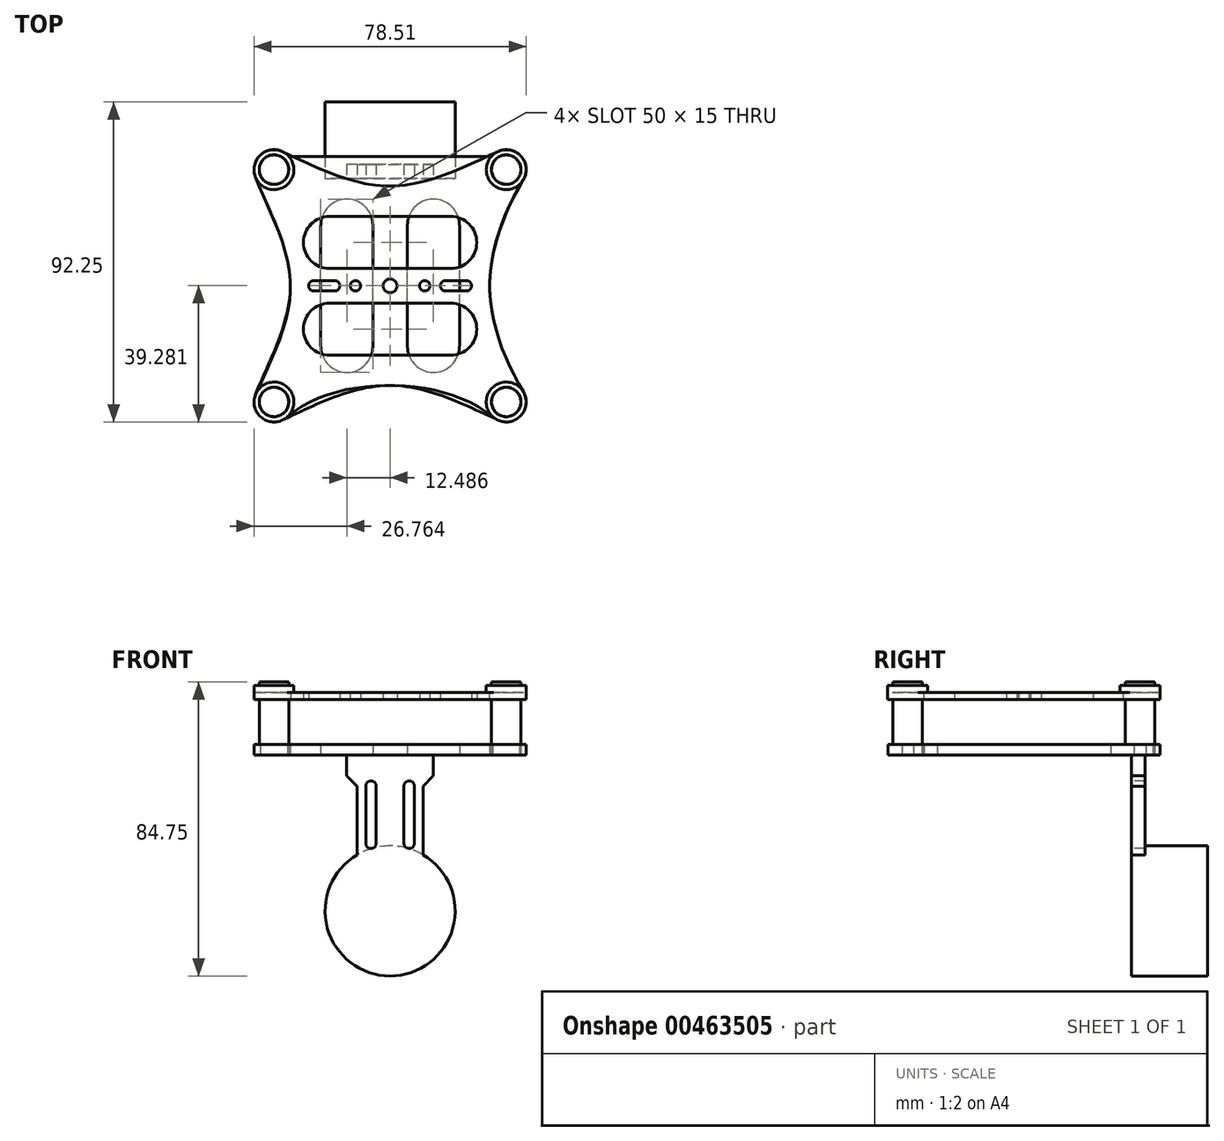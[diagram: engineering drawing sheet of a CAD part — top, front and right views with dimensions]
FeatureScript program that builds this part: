
annotation { "Feature Type Name" : "Feature", "Feature Type Description" : "" }
export const myFeature = defineFeature(function(context is Context, id is Id, definition is map)
    precondition{}
    {
        {
            var Q0;
            Q0=qCreatedBy(makeId("Top.planeOp"),FACE);
            var sketch = newSketch(context, id + "F0", { "sketchPlane" : qUnion([Q0])});
            skCircle(sketch, "E0", {"center": v(0, 0) * mm, "radius": 2 * mm});
            skCircle(sketch, "E1", {"center": v(10, 0) * mm, "radius": 1.5 * mm});
            skCircle(sketch, "E2", {"center": v(-10, 0) * mm, "radius": 1.5 * mm});
            skCircle(sketch, "E3", {"center": v(16, 0) * mm, "radius": 1.5 * mm});
            skCircle(sketch, "E4", {"center": v(22, 0) * mm, "radius": 1.5 * mm});
            skCircle(sketch, "E5", {"center": v(-16, 0) * mm, "radius": 1.5 * mm});
            skCircle(sketch, "E6", {"center": v(-22, 0) * mm, "radius": 1.5 * mm});
            skLineSegment(sketch, "E7", {"start": v(-22, 1.5) * mm, "end": v(-16, 1.5) * mm});
            skLineSegment(sketch, "E8", {"start": v(-22, -1.5) * mm, "end": v(-16, -1.5) * mm});
            skLineSegment(sketch, "E9", {"start": v(16, 1.5) * mm, "end": v(22, 1.5) * mm});
            skLineSegment(sketch, "E10", {"start": v(16, -1.5) * mm, "end": v(22, -1.5) * mm});
            skCircle(sketch, "E11", {"center": v(17.5, 12.5) * mm, "radius": 7.5 * mm});
            skCircle(sketch, "E12", {"center": v(-17.5, 12.5) * mm, "radius": 7.5 * mm});
            skCircle(sketch, "E13", {"center": v(-17.5, -12.5) * mm, "radius": 7.5 * mm});
            skCircle(sketch, "E14", {"center": v(17.5, -12.5) * mm, "radius": 7.5 * mm});
            skLineSegment(sketch, "E15", {"start": v(-17.5, 20) * mm, "end": v(17.5, 20) * mm});
            skLineSegment(sketch, "E16", {"start": v(-17.5, 5) * mm, "end": v(17.5, 5) * mm});
            skLineSegment(sketch, "E17", {"start": v(-17.5, -5) * mm, "end": v(17.5, -5) * mm});
            skLineSegment(sketch, "E18", {"start": v(-17.5, -20) * mm, "end": v(17.5, -20) * mm});
            skLineSegment(sketch, "E19.bottom", {"start": v(-39.25, 39.25) * mm, "end": v(39.25, 39.25) * mm});
            skLineSegment(sketch, "E19.top", {"start": v(-39.25, -39.25) * mm, "end": v(39.25, -39.25) * mm});
            skLineSegment(sketch, "E19.left", {"start": v(-39.25, 39.25) * mm, "end": v(-39.25, -39.25) * mm});
            skLineSegment(sketch, "E19.right", {"start": v(39.25, 39.25) * mm, "end": v(39.25, -39.25) * mm});
            skCircle(sketch, "E20", {"center": v(33.5, 33.5) * mm, "radius": 4.25 * mm});
            skCircle(sketch, "E21", {"center": v(33.5, 33.5) * mm, "radius": 5.75 * mm});
            skCircle(sketch, "E22", {"center": v(-33.5, 33.5) * mm, "radius": 4.25 * mm});
            skCircle(sketch, "E23", {"center": v(-33.5, 33.5) * mm, "radius": 5.75 * mm});
            skCircle(sketch, "E24", {"center": v(33.5, -33.5) * mm, "radius": 4.25 * mm});
            skCircle(sketch, "E25", {"center": v(33.5, -33.5) * mm, "radius": 5.75 * mm});
            skCircle(sketch, "E26", {"center": v(-33.5, -33.5) * mm, "radius": 4.25 * mm});
            skCircle(sketch, "E27", {"center": v(-33.5, -33.5) * mm, "radius": 5.75 * mm});
            skFitSpline(sketch, "E28", {"points": [v(38.41, 30.5) * mm, v(28.75, 0) * mm, v(38.43, -30.55) * mm], "startDerivative": vector(-32.2, -52.88) * mm, "endDerivative": vector(31.96, -53.39) * mm});
            skFitSpline(sketch, "E29", {"points": [v(29.85, -37.94) * mm, v(0, -28.75) * mm, v(-29.77, -37.88) * mm], "startDerivative": vector(-47.75, 39.22) * mm, "endDerivative": vector(-47.24, -40.27) * mm});
            skFitSpline(sketch, "E30", {"points": [v(-38.84, 31.37) * mm, v(-28.75, 0) * mm, v(-38.74, -31.13) * mm], "startDerivative": vector(23.05, -57.76) * mm, "endDerivative": vector(-24.73, -54.61) * mm});
            skFitSpline(sketch, "E31", {"points": [v(-31.09, 38.72) * mm, v(0, 28.75) * mm, v(31.13, 38.74) * mm], "startDerivative": vector(55, -25.43) * mm, "endDerivative": vector(55.65, 25.12) * mm});
            skSolve(sketch);
        }
        {
            var Q0;
            Q0=makeQuery(id+"F0.imprint","IMPRINT",FACE,{"disambiguationData":[TD([[makeQuery(id+"F0.imprint","IMPRINT",EDGE,{"derivedFrom":sQuery(id+"F0.wireOp",EDGE,"E24")}),-1.0]])]});
            var Q1;
            Q1=makeQuery(id+"F0.imprint","IMPRINT",FACE,{"disambiguationData":[TD([[makeQuery(id+"F0.imprint","IMPRINT",EDGE,{"derivedFrom":sQuery(id+"F0.wireOp",EDGE,"E26")}),-1.0]])]});
            var Q2;
            Q2=makeQuery(id+"F0.imprint","IMPRINT",FACE,{"disambiguationData":[TD([[makeQuery(id+"F0.imprint","IMPRINT",EDGE,{"derivedFrom":sQuery(id+"F0.wireOp",EDGE,"E22")}),-1.0]])]});
            var Q3;
            Q3=makeQuery(id+"F0.imprint","IMPRINT",FACE,{"disambiguationData":[TD([[makeQuery(id+"F0.imprint","IMPRINT",EDGE,{"derivedFrom":sQuery(id+"F0.wireOp",EDGE,"E20")}),-1.0]])]});
            var Q4;
            Q4=makeQuery(id+"F0.imprint","IMPRINT",FACE,{"disambiguationData":[TD([[makeQuery(id+"F0.imprint","IMPRINT",EDGE,{"derivedFrom":sQuery(id+"F0.wireOp",EDGE,"E0")}),-1.0]])]});
            extrude(context, id + "F1", {"entities" : qUnion([Q0, Q1, Q2, Q3, Q4]), "depth" : 2 * mm});
        }
        {
            var Q0;
            Q0=makeQuery(id+"F0.imprint","IMPRINT",FACE,{"disambiguationData":[TD([[makeQuery(id+"F0.imprint","IMPRINT",EDGE,{"derivedFrom":sQuery(id+"F0.wireOp",EDGE,"E22")}),1.0]])]});
            var Q1;
            Q1=makeQuery(id+"F0.imprint","IMPRINT",FACE,{"disambiguationData":[TD([[makeQuery(id+"F0.imprint","IMPRINT",EDGE,{"derivedFrom":sQuery(id+"F0.wireOp",EDGE,"E20")}),1.0]])]});
            var Q2;
            Q2=makeQuery(id+"F0.imprint","IMPRINT",FACE,{"disambiguationData":[TD([[makeQuery(id+"F0.imprint","IMPRINT",EDGE,{"derivedFrom":sQuery(id+"F0.wireOp",EDGE,"E24")}),1.0]])]});
            var Q3;
            Q3=makeQuery(id+"F0.imprint","IMPRINT",FACE,{"disambiguationData":[TD([[makeQuery(id+"F0.imprint","IMPRINT",EDGE,{"derivedFrom":sQuery(id+"F0.wireOp",EDGE,"E26")}),1.0]])]});
            extrude(context, id + "F2", {"entities" : qUnion([Q0, Q1, Q2, Q3]), "operationType" : NewBodyOperationType.ADD, "oppositeDirection" : true, "depth" : 16 * mm, "hasSecondDirection" : true, "secondDirectionOppositeDirection" : false, "secondDirectionDepth" : 1 * mm});
        }
        {
            var Q0;
            Q0=makeQuery(id+"F2.opExtrude","CAP_FACE",FACE,{"disambiguationData":[OSD([sQuery(id+"F0.wireOp",EDGE,"E26")])],"isStart":false});
            var sketch = newSketch(context, id + "F3", { "sketchPlane" : qUnion([Q0])});
            skCircle(sketch, "E32", {"center": v(12.51, 17.47) * mm, "radius": 7.5 * mm});
            skCircle(sketch, "E33", {"center": v(-12.49, 17.47) * mm, "radius": 7.5 * mm});
            skCircle(sketch, "E34", {"center": v(-12.49, -17.53) * mm, "radius": 7.5 * mm});
            skCircle(sketch, "E35", {"center": v(12.51, -17.53) * mm, "radius": 7.5 * mm});
            skLineSegment(sketch, "E36.bottom", {"start": v(-39.24, 39.22) * mm, "end": v(39.26, 39.22) * mm});
            skLineSegment(sketch, "E36.top", {"start": v(-39.24, -39.28) * mm, "end": v(39.26, -39.28) * mm});
            skLineSegment(sketch, "E36.left", {"start": v(-39.24, 39.22) * mm, "end": v(-39.24, -39.28) * mm});
            skLineSegment(sketch, "E36.right", {"start": v(39.26, 39.22) * mm, "end": v(39.26, -39.28) * mm});
            skCircle(sketch, "E37", {"center": v(33.51, 33.47) * mm, "radius": 4.25 * mm});
            skCircle(sketch, "E38", {"center": v(33.51, 33.47) * mm, "radius": 5.75 * mm});
            skCircle(sketch, "E39", {"center": v(-33.49, 33.47) * mm, "radius": 4.25 * mm});
            skCircle(sketch, "E40", {"center": v(-33.49, 33.47) * mm, "radius": 5.75 * mm});
            skCircle(sketch, "E41", {"center": v(33.51, -33.53) * mm, "radius": 4.25 * mm});
            skCircle(sketch, "E42", {"center": v(33.51, -33.53) * mm, "radius": 5.75 * mm});
            skCircle(sketch, "E43", {"center": v(-33.49, -33.53) * mm, "radius": 4.25 * mm});
            skCircle(sketch, "E44", {"center": v(-33.49, -33.53) * mm, "radius": 5.75 * mm});
            skFitSpline(sketch, "E45", {"points": [v(38.42, 30.48) * mm, v(28.76, -0.03) * mm, v(38.45, -30.58) * mm], "startDerivative": vector(-32.2, -52.88) * mm, "endDerivative": vector(31.96, -53.39) * mm});
            skFitSpline(sketch, "E46", {"points": [v(-38.83, 31.34) * mm, v(-28.74, -0.03) * mm, v(-38.72, -31.16) * mm], "startDerivative": vector(23.05, -57.76) * mm, "endDerivative": vector(-24.73, -54.61) * mm});
            skFitSpline(sketch, "E47", {"points": [v(-31.07, 38.69) * mm, v(0.01, 28.72) * mm, v(31.15, 38.7) * mm], "startDerivative": vector(55, -25.43) * mm, "endDerivative": vector(55.65, 25.12) * mm});
            skLineSegment(sketch, "E48", {"start": v(-29.13, -37.28) * mm, "end": v(29.15, -37.28) * mm});
            skLineSegment(sketch, "E49", {"start": v(5.01, 17.47) * mm, "end": v(5.01, -17.53) * mm});
            skLineSegment(sketch, "E50", {"start": v(20.01, 17.47) * mm, "end": v(20.01, -17.53) * mm});
            skLineSegment(sketch, "E51", {"start": v(-4.99, 17.47) * mm, "end": v(-4.99, -17.53) * mm});
            skLineSegment(sketch, "E52", {"start": v(-19.99, 17.47) * mm, "end": v(-19.99, -17.53) * mm});
            skSolve(sketch);
        }
        {
            var Q0;
            {var subQ4=sQuery(id+"F3.wireOp",EDGE,"E39");var subQ5=makeQuery(id+"F2.opExtrude","CAP_EDGE",EDGE,{"disambiguationData":[OSD([sQuery(id+"F0.wireOp",EDGE,"E26")])],"isStart":false});var subQ6=makeQuery(id+"F3.imprint","INTERSECT",VERTEX,{"disambiguationData":[OD(0.0)],"derivedFrom":[subQ5,subQ4]});Q0=makeQuery(id+"F3.imprint","IMPRINT",FACE,{"disambiguationData":[TD([[makeQuery(id+"F3.imprint","IMPRINT",EDGE,{"disambiguationData":[TD([[subQ6,-1.0]])],"derivedFrom":subQ4}),-1.0]])]});}
            var Q1;
            Q1=makeQuery(id+"F3.imprint","IMPRINT",FACE,{"disambiguationData":[TD([[makeQuery(id+"F3.imprint","IMPRINT",EDGE,{"derivedFrom":sQuery(id+"F3.wireOp",EDGE,"E37")}),-1.0]])]});
            var Q2;
            Q2=makeQuery(id+"F3.imprint","IMPRINT",FACE,{"disambiguationData":[TD([[makeQuery(id+"F3.imprint","IMPRINT",EDGE,{"derivedFrom":sQuery(id+"F3.wireOp",EDGE,"E41")}),-1.0]])]});
            var Q3;
            Q3=makeQuery(id+"F3.imprint","IMPRINT",FACE,{"disambiguationData":[TD([[makeQuery(id+"F3.imprint","IMPRINT",EDGE,{"derivedFrom":sQuery(id+"F3.wireOp",EDGE,"E43")}),-1.0]])]});
            var Q4;
            {var subQ0=sQuery(id+"F3.wireOp",EDGE,"E45");Q4=makeQuery(id+"F3.imprint","IMPRINT",FACE,{"disambiguationData":[TD([[makeQuery(id+"F3.imprint","IMPRINT",EDGE,{"derivedFrom":subQ0}),-1.0]])]});}
            extrude(context, id + "F4", {"entities" : qUnion([Q0, Q1, Q2, Q3, Q4]), "operationType" : NewBodyOperationType.ADD, "oppositeDirection" : true, "depth" : 3 * mm});
        }
        {
            var Q0;
            Q0=qCreatedBy(makeId("Front.planeOp"),FACE);
            var sketch = newSketch(context, id + "F5", { "sketchPlane" : qUnion([Q0])});
            skCircle(sketch, "E53", {"center": v(0, -61) * mm, "radius": 18.75 * mm});
            skLineSegment(sketch, "E54.bottom", {"start": v(12.5, -16) * mm, "end": v(-12.5, -16) * mm});
            skLineSegment(sketch, "E54.top", {"start": v(12.5, -61) * mm, "end": v(-12.5, -61) * mm});
            skLineSegment(sketch, "E54.left", {"start": v(12.5, -16) * mm, "end": v(12.5, -61) * mm});
            skLineSegment(sketch, "E54.right", {"start": v(-12.5, -16) * mm, "end": v(-12.5, -61) * mm});
            skLineSegment(sketch, "E55.bottom", {"start": v(9.5, -25) * mm, "end": v(-9.5, -25) * mm});
            skLineSegment(sketch, "E55.top", {"start": v(9.5, -55) * mm, "end": v(-9.5, -55) * mm});
            skLineSegment(sketch, "E55.left", {"start": v(9.5, -25) * mm, "end": v(9.5, -55) * mm});
            skLineSegment(sketch, "E55.right", {"start": v(-9.5, -25) * mm, "end": v(-9.5, -55) * mm});
            skLineSegment(sketch, "E56", {"start": v(9.5, -25) * mm, "end": v(12.5, -22) * mm});
            skLineSegment(sketch, "E57", {"start": v(-9.5, -25) * mm, "end": v(-12.5, -22) * mm});
            skCircle(sketch, "E58", {"center": v(5.5, -25) * mm, "radius": 1.5 * mm});
            skCircle(sketch, "E59", {"center": v(5.5, -41.51) * mm, "radius": 1.5 * mm});
            skCircle(sketch, "E60", {"center": v(-5.5, -25) * mm, "radius": 1.5 * mm});
            skCircle(sketch, "E61", {"center": v(-5.5, -41.51) * mm, "radius": 1.5 * mm});
            skLineSegment(sketch, "E62", {"start": v(9.5, -42.37) * mm, "end": v(-9.5, -42.13) * mm, "construction": true});
            skLineSegment(sketch, "E63", {"start": v(7, -25) * mm, "end": v(7, -41.51) * mm});
            skLineSegment(sketch, "E64", {"start": v(4, -25) * mm, "end": v(4, -41.51) * mm});
            skLineSegment(sketch, "E65", {"start": v(-4, -25) * mm, "end": v(-4, -41.51) * mm});
            skLineSegment(sketch, "E66", {"start": v(-7, -25) * mm, "end": v(-7, -41.51) * mm});
            skSolve(sketch);
        }
        {
            var Q0;
            {var subQ6=sQuery(id+"F5.wireOp",EDGE,"E54.bottom");Q0=makeQuery(id+"F5.imprint","IMPRINT",FACE,{"disambiguationData":[TD([[makeQuery(id+"F5.imprint","IMPRINT",EDGE,{"derivedFrom":subQ6}),1.0]])]});}
            var Q1;
            {var subQ6=sQuery(id+"F5.wireOp",EDGE,"E64");Q1=makeQuery(id+"F5.imprint","IMPRINT",FACE,{"disambiguationData":[TD([[makeQuery(id+"F5.imprint","IMPRINT",EDGE,{"derivedFrom":subQ6}),-1.0]])]});}
            var Q2;
            {var subQ0=sQuery(id+"F5.wireOp",EDGE,"E66");Q2=makeQuery(id+"F5.imprint","IMPRINT",FACE,{"disambiguationData":[TD([[makeQuery(id+"F5.imprint","IMPRINT",EDGE,{"derivedFrom":subQ0}),-1.0]])]});}
            var Q3;
            {var subQ0=sQuery(id+"F5.wireOp",EDGE,"E63");Q3=makeQuery(id+"F5.imprint","IMPRINT",FACE,{"disambiguationData":[TD([[makeQuery(id+"F5.imprint","IMPRINT",EDGE,{"derivedFrom":subQ0}),1.0]])]});}
            var Q4;
            {var subQ0=sQuery(id+"F5.wireOp",EDGE,"E55.top");Q4=makeQuery(id+"F5.imprint","IMPRINT",FACE,{"disambiguationData":[TD([[makeQuery(id+"F5.imprint","IMPRINT",EDGE,{"derivedFrom":subQ0}),-1.0]])]});}
            var Q5;
            {var subQ0=sQuery(id+"F5.wireOp",EDGE,"E54.top");Q5=makeQuery(id+"F5.imprint","IMPRINT",FACE,{"disambiguationData":[TD([[makeQuery(id+"F5.imprint","IMPRINT",EDGE,{"derivedFrom":subQ0}),-1.0]])]});}
            var Q6;
            {var subQ5=sQuery(id+"F5.wireOp",EDGE,"E54.top");Q6=makeQuery(id+"F5.imprint","IMPRINT",FACE,{"disambiguationData":[TD([[makeQuery(id+"F5.imprint","IMPRINT",EDGE,{"derivedFrom":subQ5}),1.0]])]});}
            extrude(context, id + "F6", {"entities" : qUnion([Q0, Q1, Q2, Q3, Q4, Q5, Q6]), "operationType" : NewBodyOperationType.ADD, "oppositeDirection" : true, "depth" : 35 * mm, "hasSecondDirection" : true, "secondDirectionOppositeDirection" : true, "secondDirectionDepth" : 31 * mm});
        }
        {
            var Q0;
            Q0=makeQuery(id+"F6.opExtrude","CAP_FACE",FACE,{"disambiguationData":[OSD([sQuery(id+"F5.wireOp",EDGE,"E53"),sQuery(id+"F5.wireOp",EDGE,"E54.bottom"),sQuery(id+"F5.wireOp",EDGE,"E54.left"),sQuery(id+"F5.wireOp",EDGE,"E54.right"),sQuery(id+"F5.wireOp",EDGE,"E55.left"),sQuery(id+"F5.wireOp",EDGE,"E55.right"),sQuery(id+"F5.wireOp",EDGE,"E56"),sQuery(id+"F5.wireOp",EDGE,"E57"),sQuery(id+"F5.wireOp",EDGE,"E58"),sQuery(id+"F5.wireOp",EDGE,"E59"),sQuery(id+"F5.wireOp",EDGE,"E60"),sQuery(id+"F5.wireOp",EDGE,"E61"),sQuery(id+"F5.wireOp",EDGE,"E63"),sQuery(id+"F5.wireOp",EDGE,"E64"),sQuery(id+"F5.wireOp",EDGE,"E65"),sQuery(id+"F5.wireOp",EDGE,"E66")])],"isStart":false});
            var sketch = newSketch(context, id + "F7", { "sketchPlane" : qUnion([Q0])});
            skCircle(sketch, "E67", {"center": v(0, -61) * mm, "radius": 18.75 * mm});
            skSolve(sketch);
        }
        {
            var Q0;
            {var subQ0=sQuery(id+"F7.wireOp",EDGE,"E67");var subQ1=makeQuery(id+"F7.imprint","INTERSECT",VERTEX,{"derivedFrom":[makeQuery(id+"F6.opExtrude","CAP_EDGE",EDGE,{"disambiguationData":[OSD([sQuery(id+"F5.wireOp",EDGE,"E55.right")])],"isStart":false}),subQ0]});var subQ2=makeQuery(id+"F7.imprint","INTERSECT",VERTEX,{"derivedFrom":[makeQuery(id+"F6.opExtrude","CAP_EDGE",EDGE,{"disambiguationData":[OSD([sQuery(id+"F5.wireOp",EDGE,"E61")])],"isStart":false}),subQ0]});Q0=makeQuery(id+"F7.imprint","IMPRINT",FACE,{"disambiguationData":[TD([[makeQuery(id+"F7.imprint","IMPRINT",EDGE,{"disambiguationData":[TD([[subQ1,-1.0],[subQ2,1.0]])],"derivedFrom":subQ0}),1.0]])]});}
            extrude(context, id + "F8", {"entities" : qUnion([Q0]), "operationType" : NewBodyOperationType.ADD, "depth" : 18 * mm});
        }
        {
            var Q0;
            Q0=makeQuery(id+"F0.imprint","IMPRINT",FACE,{"disambiguationData":[TD([[makeQuery(id+"F0.imprint","IMPRINT",EDGE,{"derivedFrom":sQuery(id+"F0.wireOp",EDGE,"E26")}),-1.0]])]});
            var Q1;
            Q1=makeQuery(id+"F0.imprint","IMPRINT",FACE,{"disambiguationData":[TD([[makeQuery(id+"F0.imprint","IMPRINT",EDGE,{"derivedFrom":sQuery(id+"F0.wireOp",EDGE,"E24")}),-1.0]])]});
            var Q2;
            Q2=makeQuery(id+"F0.imprint","IMPRINT",FACE,{"disambiguationData":[TD([[makeQuery(id+"F0.imprint","IMPRINT",EDGE,{"derivedFrom":sQuery(id+"F0.wireOp",EDGE,"E22")}),-1.0]])]});
            var Q3;
            Q3=makeQuery(id+"F0.imprint","IMPRINT",FACE,{"disambiguationData":[TD([[makeQuery(id+"F0.imprint","IMPRINT",EDGE,{"derivedFrom":sQuery(id+"F0.wireOp",EDGE,"E20")}),-1.0]])]});
            var Q4;
            Q4=makeQuery(id+"F2.opExtrude","CAP_FACE",FACE,{"disambiguationData":[OSD([sQuery(id+"F0.wireOp",EDGE,"E26")])],"isStart":true});
            var Q5;
            Q5=makeQuery(id+"F2.opExtrude","CAP_FACE",FACE,{"disambiguationData":[OSD([sQuery(id+"F0.wireOp",EDGE,"E22")])],"isStart":true});
            var Q6;
            Q6=makeQuery(id+"F2.opExtrude","CAP_FACE",FACE,{"disambiguationData":[OSD([sQuery(id+"F0.wireOp",EDGE,"E20")])],"isStart":true});
            var Q7;
            Q7=makeQuery(id+"F2.opExtrude","CAP_FACE",FACE,{"disambiguationData":[OSD([sQuery(id+"F0.wireOp",EDGE,"E24")])],"isStart":true});
            extrude(context, id + "F9", {"entities" : qUnion([Q0, Q1, Q2, Q3, Q4, Q5, Q6, Q7]), "operationType" : NewBodyOperationType.ADD, "depth" : 4 * mm, "offsetDistance" : 25 * mm});
        }
    });
